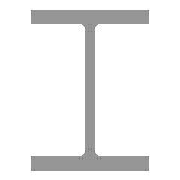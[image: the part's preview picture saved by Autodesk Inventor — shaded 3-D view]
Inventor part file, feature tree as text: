
AUTODESK INVENTOR PART (.ipt)
format: ipt  version: 2016 (Build 200138000, 138)  size: 157,184 bytes
history: native  units: mm (DEFAULTED — no unit token found)
features: plane x5, other x3, sketch x3, extrude x1
ambient origin geometry x8: Origin, YZ Plane, XZ Plane, XY Plane, X Axis, Y Axis, Z Axis, Center Point
bodies: Solid1 (feature_tree), Body (feature_tree)
feature tree (12):
  other  "Driven Length"
  other  "Start plane"
  other  "End plane"
  extrude  "Extrusion2"  Depth=31.75mm
  plane  "Work Plane4"
  plane  "Work Plane5"
  plane  "Work Plane6"
  plane  "Work Plane7"
  sketch  "Sketch4"  dims[d1=144.78mm d2=31.75mm]
  plane  "Work Plane3"
  sketch  "Sketch5"  dims[d3=132.08mm]
  sketch  "Sketch6"  dims[d4=9.5885mm d5=4032.25mm d6=0.0mm d11=-0.0mm d12=4032.25mm d13=12.7mm d14=90.0deg d15=4032.25mm d29=50.8mm d30=0.0mm d31=2016.125mm d32=2016.125mm d33=1008.0625mm d34=1008.0625mm]
